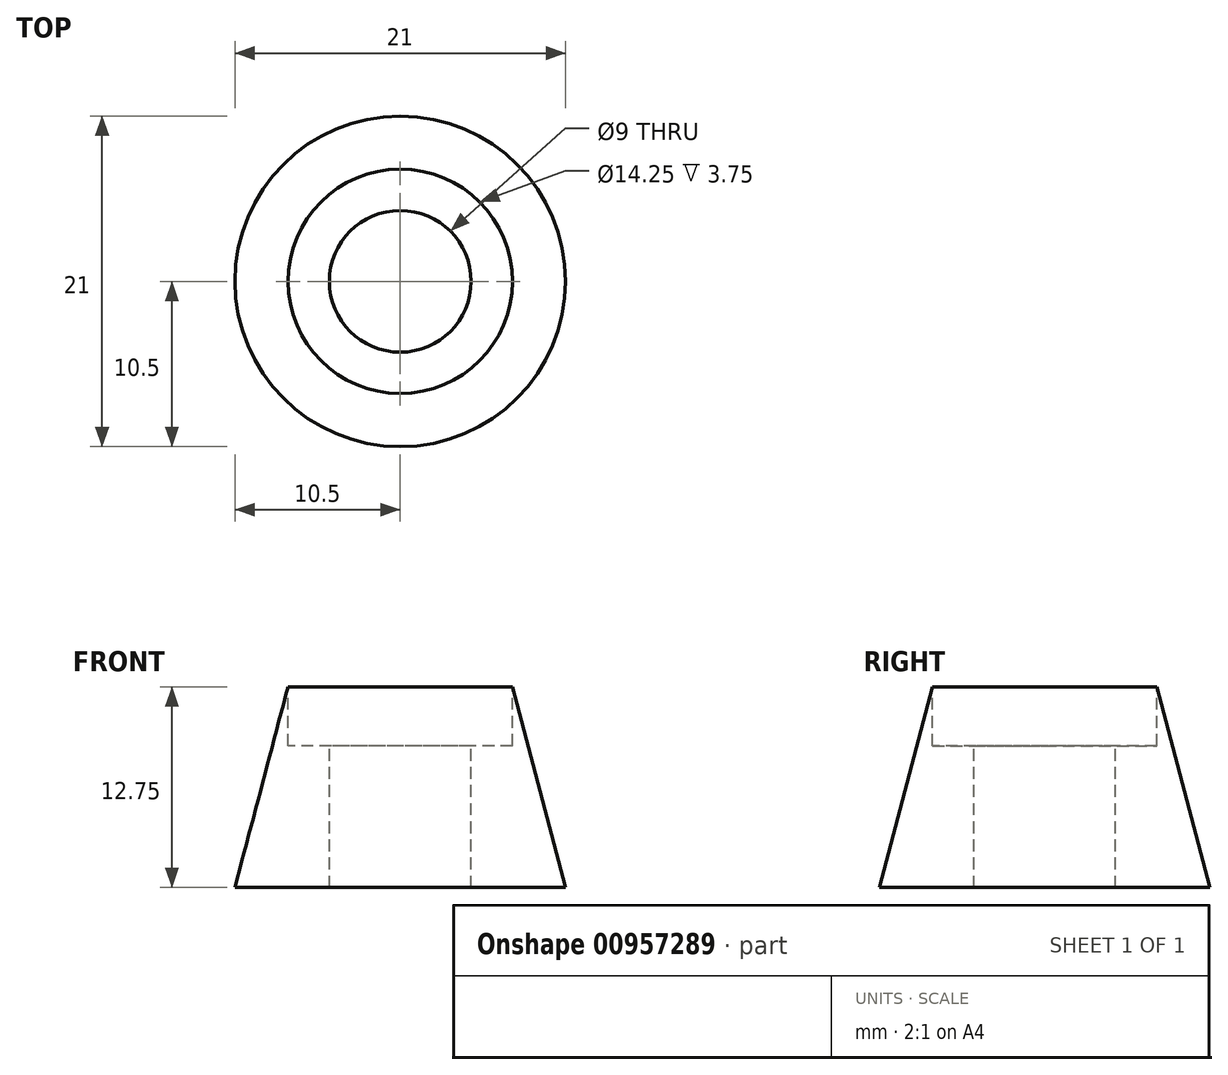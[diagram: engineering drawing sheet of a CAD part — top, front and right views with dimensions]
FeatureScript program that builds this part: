
annotation { "Feature Type Name" : "Feature", "Feature Type Description" : "" }
export const myFeature = defineFeature(function(context is Context, id is Id, definition is map)
    precondition{}
    {
        {
            var Q0;
            Q0=qCreatedBy(makeId("Top.planeOp"),FACE);
            var sketch = newSketch(context, id + "F0", { "sketchPlane" : qUnion([Q0])});
            skCircle(sketch, "E0", {"center": v(0, 0) * mm, "radius": 10.5 * mm});
            skSolve(sketch);
        }
        {
            var Q0;
            Q0=qCreatedBy(makeId("Top.planeOp"),FACE);
            cPlane(context, id + "F1", {"entities" : qUnion([Q0]), "cplaneType" : CPlaneType.OFFSET, "offset" : 17 * mm, "width" : 150 * mm, "height" : 150 * mm});
        }
        {
            var Q0;
            Q0=qCreatedBy(id+"F1.planeOp",FACE);
            var sketch = newSketch(context, id + "F2", { "sketchPlane" : qUnion([Q0])});
            skCircle(sketch, "E1", {"center": v(0, 0) * mm, "radius": 6 * mm});
            skSolve(sketch);
        }
        {
            var Q0;
            Q0=makeQuery(id+"F2.imprint","IMPRINT",FACE,{"disambiguationData":[TD([[makeQuery(id+"F2.imprint","IMPRINT",EDGE,{"derivedFrom":sQuery(id+"F2.wireOp",EDGE,"E1")}),1.0]])]});
            var Q1;
            Q1=makeQuery(id+"F0.imprint","IMPRINT",FACE,{"disambiguationData":[TD([[makeQuery(id+"F0.imprint","IMPRINT",EDGE,{"derivedFrom":sQuery(id+"F0.wireOp",EDGE,"E0")}),1.0]])]});
            loft(context, id + "F3", {"sheetProfilesArray" : [{ "sheetProfileEntities" : qUnion([Q0]) }, { "sheetProfileEntities" : qUnion([Q1]) }]});
        }
        {
            var Q0;
            Q0=qCreatedBy(id+"F1.planeOp",FACE);
            var sketch = newSketch(context, id + "F4", { "sketchPlane" : qUnion([Q0])});
            skPoint(sketch, "E2", {"position": v(0, 0) * mm});
            skSolve(sketch);
        }
        {
            var Q0;
            Q0=sQuery(id+"F4.wireOp",VERTEX,"E2");
            var Q1;
            Q1=makeQuery(id+"F3.opLoft","SWEPT_BODY",BODY,{"disambiguationData":[OSD([makeQuery(id+"F0.imprint","IMPRINT",FACE,{"disambiguationData":[TD([[makeQuery(id+"F0.imprint","IMPRINT",EDGE,{"derivedFrom":sQuery(id+"F0.wireOp",EDGE,"E0")}),1.0]])]}),makeQuery(id+"F2.imprint","IMPRINT",FACE,{"disambiguationData":[TD([[makeQuery(id+"F2.imprint","IMPRINT",EDGE,{"derivedFrom":sQuery(id+"F2.wireOp",EDGE,"E1")}),1.0]])]})])]});
            hole(context, id + "F5", {"style" : HoleStyle.C_BORE, "endStyle" : HoleEndStyle.THROUGH, "standardTappedOrClearance" : lookupTablePath({ "fit" : "Normal", "standard" : "ISO", "size" : "M8", "type" : "Clearance" }), "standardBlindInLast" : lookupTablePath({ "fit" : "Normal", "standard" : "ISO", "engagement" : "75%", "pitch" : "1.25 mm", "size" : "M8", "type" : "Clearance & tapped" }), "holeDiameter" : 9 * mm, "cBoreDiameter" : 14.25 * mm, "cBoreDepth" : 8 * mm, "majorDiameter" : 4 * mm, "isTappedThrough" : true, "tappedDepth" : 7.9 * mm, "tapClearance" : 3, "startFromSketch" : true, "locations" : qUnion([Q0]), "scope" : qUnion([Q1])});
        }
    });
